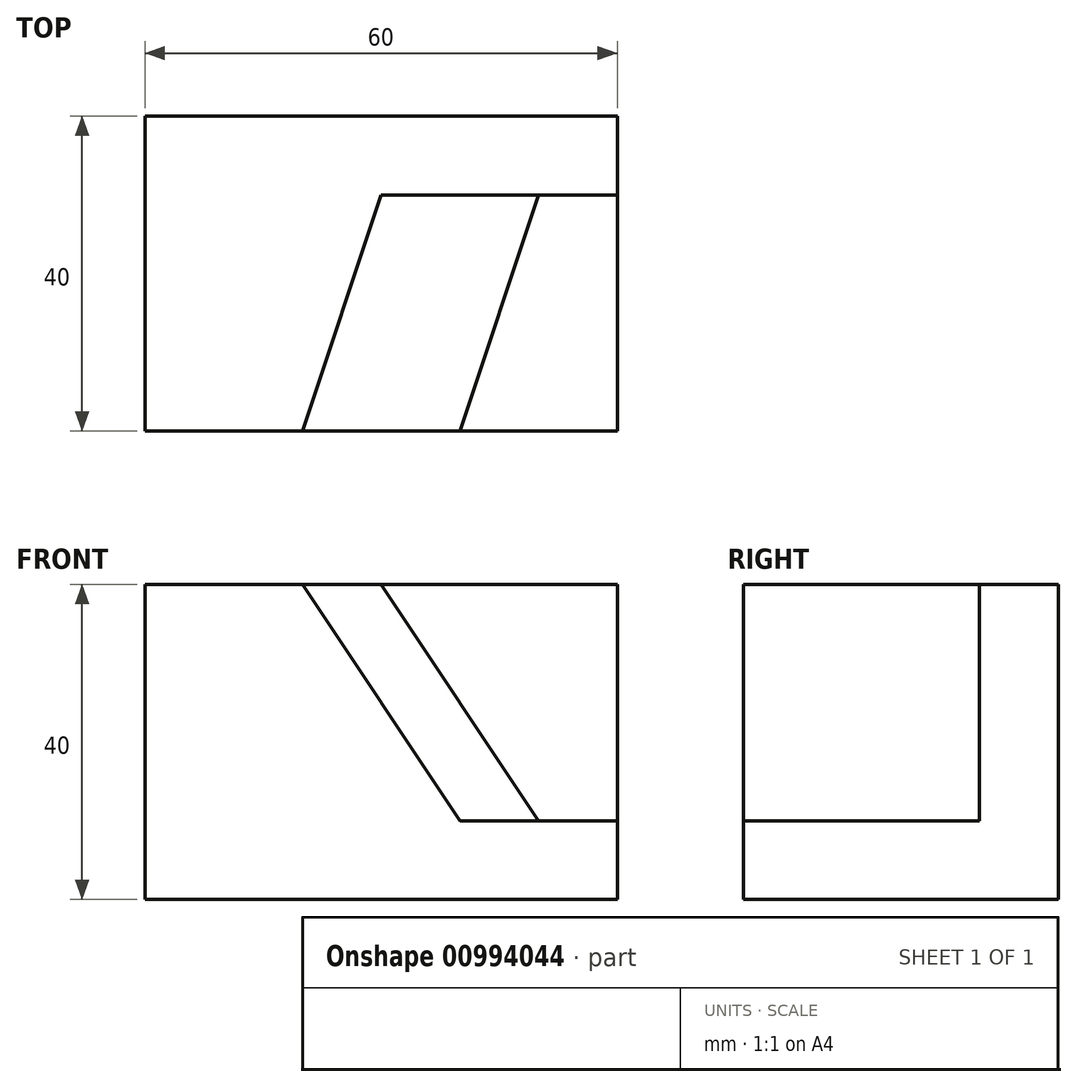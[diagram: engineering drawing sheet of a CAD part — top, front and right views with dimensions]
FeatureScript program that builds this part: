
annotation { "Feature Type Name" : "Feature", "Feature Type Description" : "" }
export const myFeature = defineFeature(function(context is Context, id is Id, definition is map)
    precondition{}
    {
        {
            var Q0;
            Q0=qCreatedBy(makeId("Top.planeOp"),FACE);
            var sketch = newSketch(context, id + "F0", { "sketchPlane" : qUnion([Q0])});
            skLineSegment(sketch, "E0.bottom", {"start": v(0, 0) * mm, "end": v(60, 0) * mm});
            skLineSegment(sketch, "E0.top", {"start": v(0, 40) * mm, "end": v(60, 40) * mm});
            skLineSegment(sketch, "E0.left", {"start": v(0, 0) * mm, "end": v(0, 40) * mm});
            skLineSegment(sketch, "E0.right", {"start": v(60, 0) * mm, "end": v(60, 40) * mm});
            skSolve(sketch);
        }
        {
            var Q0;
            Q0=makeQuery(id+"F0.imprint","IMPRINT",FACE,{"disambiguationData":[TD([[makeQuery(id+"F0.imprint","IMPRINT",EDGE,{"derivedFrom":sQuery(id+"F0.wireOp",EDGE,"E0.bottom")}),1.0]])]});
            extrude(context, id + "F1", {"entities" : qUnion([Q0]), "depth" : 10 * mm, "offsetDistance" : 25 * mm});
        }
        {
            var Q0;
            Q0=makeQuery(id+"F1.opExtrude","CAP_FACE",FACE,{"disambiguationData":[OSD([sQuery(id+"F0.wireOp",EDGE,"E0.bottom"),sQuery(id+"F0.wireOp",EDGE,"E0.top"),sQuery(id+"F0.wireOp",EDGE,"E0.left"),sQuery(id+"F0.wireOp",EDGE,"E0.right")])],"isStart":false});
            cPlane(context, id + "F2", {"entities" : qUnion([Q0]), "cplaneType" : CPlaneType.OFFSET, "offset" : 30 * mm, "width" : 150 * mm, "height" : 150 * mm});
        }
        {
            var Q0;
            Q0=qCreatedBy(id+"F2.planeOp",FACE);
            var sketch = newSketch(context, id + "F3", { "sketchPlane" : qUnion([Q0])});
            skLineSegment(sketch, "E1.0", {"start": v(0, 0) * mm, "end": v(0, 40) * mm});
            skLineSegment(sketch, "E2.0", {"start": v(0, 40) * mm, "end": v(60, 40) * mm});
            skLineSegment(sketch, "E3.0", {"start": v(60, 0) * mm, "end": v(60, 40) * mm});
            skLineSegment(sketch, "E4.0", {"start": v(0, 0) * mm, "end": v(60, 0) * mm});
            skLineSegment(sketch, "E5.0", {"start": v(30, 30) * mm, "end": v(60, 30) * mm});
            skLineSegment(sketch, "E6", {"start": v(40, 0) * mm, "end": v(50, 30) * mm});
            skLineSegment(sketch, "E7", {"start": v(20, 0) * mm, "end": v(30, 30) * mm});
            skSolve(sketch);
        }
        {
            var Q0;
            Q0=makeQuery(id+"F1.opExtrude","CAP_FACE",FACE,{"disambiguationData":[OSD([sQuery(id+"F0.wireOp",EDGE,"E0.bottom"),sQuery(id+"F0.wireOp",EDGE,"E0.top"),sQuery(id+"F0.wireOp",EDGE,"E0.left"),sQuery(id+"F0.wireOp",EDGE,"E0.right")])],"isStart":false});
            var sketch = newSketch(context, id + "F4", { "sketchPlane" : qUnion([Q0])});
            skLineSegment(sketch, "E8.0.0", {"start": v(60, 30) * mm, "end": v(50, 30) * mm});
            skLineSegment(sketch, "E8.0.1", {"start": v(50, 30) * mm, "end": v(40, 0) * mm});
            skLineSegment(sketch, "E8.0.2", {"start": v(40, 0) * mm, "end": v(60, 0) * mm});
            skLineSegment(sketch, "E8.0.3", {"start": v(60, 0) * mm, "end": v(60, 30) * mm});
            skSolve(sketch);
        }
        {
            var Q1;
            {var subQ1=sQuery(id+"F3.wireOp",EDGE,"E1.0");Q1=makeQuery(id+"F3.imprint","IMPRINT",FACE,{"disambiguationData":[TD([[makeQuery(id+"F3.imprint","IMPRINT",EDGE,{"derivedFrom":subQ1}),-1.0]])]});}
            var Q2;
            {var subQ4=sQuery(id+"F4.wireOp",EDGE,"E8.0.0");Q2=makeQuery(id+"F4.imprint","IMPRINT",FACE,{"disambiguationData":[TD([[makeQuery(id+"F4.imprint","IMPRINT",EDGE,{"derivedFrom":subQ4}),-1.0]])]});}
            var Q3;
            Q3=sQuery(id+"F3.wireOp",VERTEX,"E5.0.end");
            var Q4;
            Q4=sQuery(id+"F4.wireOp",VERTEX,"E8.0.0.start");
            loft(context, id + "F5", {"operationType" : NewBodyOperationType.ADD, "sheetProfilesArray" : [{ "sheetProfileEntities" : qUnion([Q1]) }, { "sheetProfileEntities" : qUnion([Q2]) }], "matchConnections" : true, "connections" : [{ "connectionEntities" : qUnion([Q3, Q4]), "connectionEdgeQueries" : qUnion([]), "connectionEdgeParameters" : [] }]});
        }
    });
